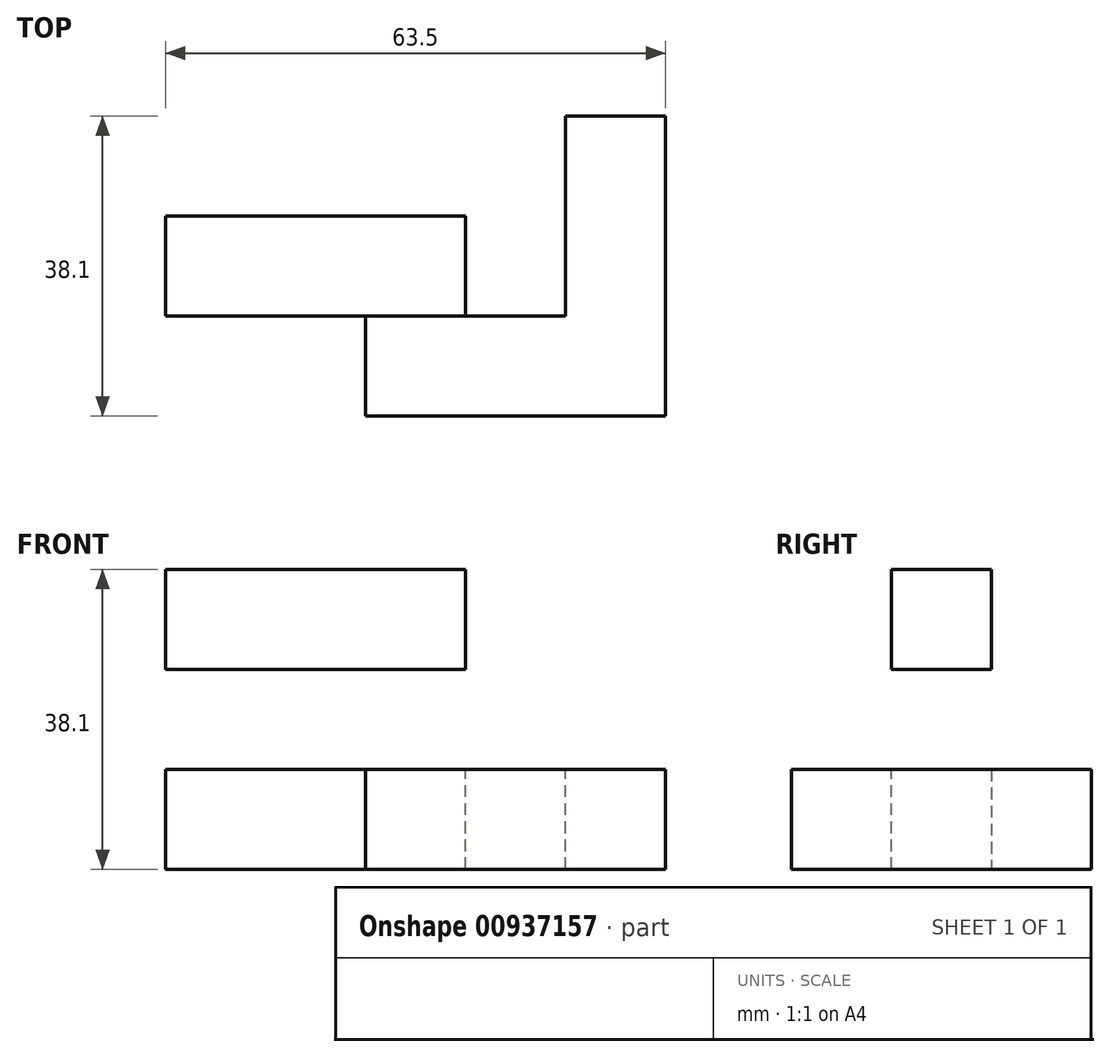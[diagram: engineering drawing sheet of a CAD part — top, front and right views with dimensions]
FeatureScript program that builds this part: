
annotation { "Feature Type Name" : "Feature", "Feature Type Description" : "" }
export const myFeature = defineFeature(function(context is Context, id is Id, definition is map)
    precondition{}
    {
        {
            var Q0;
            Q0=qCreatedBy(makeId("Front.planeOp"),FACE);
            var sketch = newSketch(context, id + "F0", { "sketchPlane" : qUnion([Q0])});
            skLineSegment(sketch, "E0.bottom", {"start": v(-30.4, 23.24) * mm, "end": v(-17.7, 23.24) * mm});
            skLineSegment(sketch, "E0.top", {"start": v(-30.4, 35.94) * mm, "end": v(-17.7, 35.94) * mm});
            skLineSegment(sketch, "E0.left", {"start": v(-30.4, 23.24) * mm, "end": v(-30.4, 35.94) * mm});
            skLineSegment(sketch, "E0.right", {"start": v(-17.7, 23.24) * mm, "end": v(-17.7, 35.94) * mm});
            skLineSegment(sketch, "E1.bottom", {"start": v(-30.4, 23.24) * mm, "end": v(-43.1, 23.24) * mm});
            skLineSegment(sketch, "E1.top", {"start": v(-30.4, 35.94) * mm, "end": v(-43.1, 35.94) * mm});
            skLineSegment(sketch, "E1.right", {"start": v(-43.1, 23.24) * mm, "end": v(-43.1, 35.94) * mm});
            skLineSegment(sketch, "E2.bottom", {"start": v(-43.1, 23.24) * mm, "end": v(-55.8, 23.24) * mm});
            skLineSegment(sketch, "E2.top", {"start": v(-43.1, 35.94) * mm, "end": v(-55.8, 35.94) * mm});
            skLineSegment(sketch, "E2.right", {"start": v(-55.8, 23.24) * mm, "end": v(-55.8, 35.94) * mm});
            skLineSegment(sketch, "E3.bottom", {"start": v(-55.8, 23.24) * mm, "end": v(-43.1, 23.24) * mm});
            skLineSegment(sketch, "E3.top", {"start": v(-55.8, 10.54) * mm, "end": v(-43.1, 10.54) * mm});
            skLineSegment(sketch, "E3.left", {"start": v(-55.8, 23.24) * mm, "end": v(-55.8, 10.54) * mm});
            skLineSegment(sketch, "E3.right", {"start": v(-43.1, 23.24) * mm, "end": v(-43.1, 10.54) * mm});
            skLineSegment(sketch, "E4.top", {"start": v(-55.8, -2.16) * mm, "end": v(-43.1, -2.16) * mm});
            skLineSegment(sketch, "E4.left", {"start": v(-55.8, 10.54) * mm, "end": v(-55.8, -2.16) * mm});
            skLineSegment(sketch, "E4.right", {"start": v(-43.1, 10.54) * mm, "end": v(-43.1, -2.16) * mm});
            skLineSegment(sketch, "E5.bottom", {"start": v(-43.1, -2.16) * mm, "end": v(-30.4, -2.16) * mm});
            skLineSegment(sketch, "E5.top", {"start": v(-43.1, 10.54) * mm, "end": v(-30.4, 10.54) * mm});
            skLineSegment(sketch, "E5.left", {"start": v(-43.1, -2.16) * mm, "end": v(-43.1, 10.54) * mm});
            skLineSegment(sketch, "E5.right", {"start": v(-30.4, -2.16) * mm, "end": v(-30.4, 10.54) * mm});
            skLineSegment(sketch, "E6.bottom", {"start": v(-30.4, -2.16) * mm, "end": v(-17.7, -2.16) * mm});
            skLineSegment(sketch, "E6.top", {"start": v(-30.4, 10.54) * mm, "end": v(-17.7, 10.54) * mm});
            skLineSegment(sketch, "E6.right", {"start": v(-17.7, -2.16) * mm, "end": v(-17.7, 10.54) * mm});
            skLineSegment(sketch, "E7.bottom", {"start": v(-17.7, -2.16) * mm, "end": v(-5, -2.16) * mm});
            skLineSegment(sketch, "E7.top", {"start": v(-17.7, 10.54) * mm, "end": v(-5, 10.54) * mm});
            skLineSegment(sketch, "E7.right", {"start": v(-5, -2.16) * mm, "end": v(-5, 10.54) * mm});
            skLineSegment(sketch, "E8.bottom", {"start": v(-5, -2.16) * mm, "end": v(7.7, -2.16) * mm});
            skLineSegment(sketch, "E8.top", {"start": v(-5, 10.54) * mm, "end": v(7.7, 10.54) * mm});
            skLineSegment(sketch, "E8.right", {"start": v(7.7, -2.16) * mm, "end": v(7.7, 10.54) * mm});
            skSolve(sketch);
        }
        {
            var Q0;
            Q0=makeQuery(id+"F0.imprint","IMPRINT",FACE,{"disambiguationData":[TD([[makeQuery(id+"F0.imprint","IMPRINT",EDGE,{"derivedFrom":sQuery(id+"F0.wireOp",EDGE,"E7.bottom")}),1.0]])]});
            var Q1;
            Q1=makeQuery(id+"F0.imprint","IMPRINT",FACE,{"disambiguationData":[TD([[makeQuery(id+"F0.imprint","IMPRINT",EDGE,{"derivedFrom":sQuery(id+"F0.wireOp",EDGE,"E6.bottom")}),1.0]])]});
            var Q2;
            Q2=makeQuery(id+"F0.imprint","IMPRINT",FACE,{"disambiguationData":[TD([[makeQuery(id+"F0.imprint","IMPRINT",EDGE,{"derivedFrom":sQuery(id+"F0.wireOp",EDGE,"E8.bottom")}),1.0]])]});
            extrude(context, id + "F1", {"entities" : qUnion([Q0, Q1, Q2]), "depth" : 12.7 * mm, "offsetDistance" : 25.4 * mm});
        }
        {
            var Q0;
            Q0=makeQuery(id+"F0.imprint","IMPRINT",FACE,{"disambiguationData":[TD([[makeQuery(id+"F0.imprint","IMPRINT",EDGE,{"derivedFrom":sQuery(id+"F0.wireOp",EDGE,"E6.bottom")}),1.0]])]});
            var Q1;
            Q1=makeQuery(id+"F0.imprint","IMPRINT",FACE,{"disambiguationData":[TD([[makeQuery(id+"F0.imprint","IMPRINT",EDGE,{"derivedFrom":sQuery(id+"F0.wireOp",EDGE,"E5.bottom")}),1.0]])]});
            var Q2;
            Q2=makeQuery(id+"F0.imprint","IMPRINT",FACE,{"disambiguationData":[TD([[makeQuery(id+"F0.imprint","IMPRINT",EDGE,{"derivedFrom":sQuery(id+"F0.wireOp",EDGE,"E3.top")}),-1.0]])]});
            var Q3;
            Q3=makeQuery(id+"F0.imprint","IMPRINT",FACE,{"disambiguationData":[TD([[makeQuery(id+"F0.imprint","IMPRINT",EDGE,{"derivedFrom":sQuery(id+"F0.wireOp",EDGE,"E3.bottom")}),-1.0]])]});
            var Q4;
            Q4=makeQuery(id+"F0.imprint","IMPRINT",FACE,{"disambiguationData":[TD([[makeQuery(id+"F0.imprint","IMPRINT",EDGE,{"derivedFrom":sQuery(id+"F0.wireOp",EDGE,"E2.top")}),1.0]])]});
            var Q5;
            Q5=makeQuery(id+"F0.imprint","IMPRINT",FACE,{"disambiguationData":[TD([[makeQuery(id+"F0.imprint","IMPRINT",EDGE,{"derivedFrom":sQuery(id+"F0.wireOp",EDGE,"E1.bottom")}),-1.0]])]});
            var Q6;
            Q6=makeQuery(id+"F0.imprint","IMPRINT",FACE,{"disambiguationData":[TD([[makeQuery(id+"F0.imprint","IMPRINT",EDGE,{"derivedFrom":sQuery(id+"F0.wireOp",EDGE,"E0.bottom")}),1.0]])]});
            extrude(context, id + "F2", {"entities" : qUnion([Q0, Q1, Q2, Q3, Q4, Q5, Q6]), "operationType" : NewBodyOperationType.ADD, "oppositeDirection" : true, "depth" : 12.7 * mm, "offsetDistance" : 25.4 * mm});
        }
        {
            var Q0;
            Q0=makeQuery(id+"F0.imprint","IMPRINT",FACE,{"disambiguationData":[TD([[makeQuery(id+"F0.imprint","IMPRINT",EDGE,{"derivedFrom":sQuery(id+"F0.wireOp",EDGE,"E8.bottom")}),1.0]])]});
            extrude(context, id + "F3", {"entities" : qUnion([Q0]), "operationType" : NewBodyOperationType.ADD, "oppositeDirection" : true, "depth" : 25.4 * mm, "offsetDistance" : 25.4 * mm});
        }
    });
